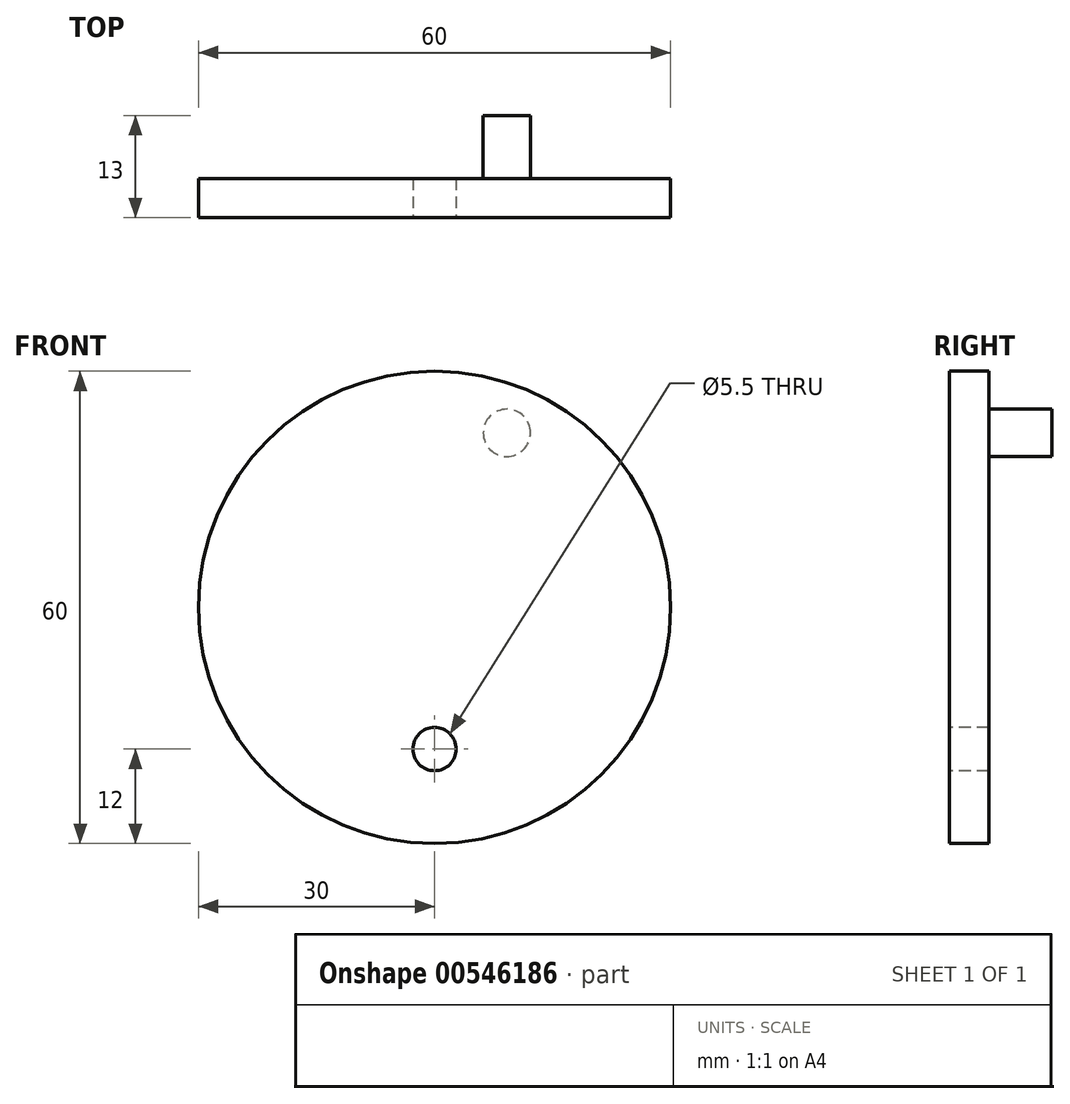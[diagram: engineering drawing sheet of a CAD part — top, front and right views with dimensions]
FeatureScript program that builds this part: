
annotation { "Feature Type Name" : "Feature", "Feature Type Description" : "" }
export const myFeature = defineFeature(function(context is Context, id is Id, definition is map)
    precondition{}
    {
        {
            var Q0;
            Q0=qCreatedBy(makeId("Front.planeOp"),FACE);
            var sketch = newSketch(context, id + "F0", { "sketchPlane" : qUnion([Q0])});
            skCircle(sketch, "E0", {"center": v(0, 0) * mm, "radius": 30 * mm});
            skSolve(sketch);
        }
        {
            var Q0;
            Q0 = qSketchRegion(id + "F0", true);
            extrude(context, id + "F1", {"entities" : qUnion([Q0]), "depth" : 5 * mm, "offsetDistance" : 25 * mm});
        }
        {
            var Q0;
            Q0=makeQuery(id+"F1.opExtrude","CAP_FACE",FACE,{"disambiguationData":[OSD([sQuery(id+"F0.wireOp",EDGE,"E0")])],"isStart":false});
            var sketch = newSketch(context, id + "F2", { "sketchPlane" : qUnion([Q0])});
            skLineSegment(sketch, "E1", {"start": v(0, 0) * mm, "end": v(0, -18) * mm});
            skCircle(sketch, "E2", {"center": v(0, -18) * mm, "radius": 2.75 * mm});
            skSolve(sketch);
        }
        {
            var Q0;
            Q0=makeQuery(id+"F2.imprint","IMPRINT",FACE,{"disambiguationData":[TD([[makeQuery(id+"F2.imprint","IMPRINT",EDGE,{"derivedFrom":sQuery(id+"F2.wireOp",EDGE,"tPdcvkMc-Bunr-VTIq-aCWn-UR4HdvMpEIR7")}),1.0]])]});
            var Q1;
            Q1=makeQuery(id+"F2.imprint","IMPRINT",FACE,{"disambiguationData":[TD([[makeQuery(id+"F2.imprint","IMPRINT",EDGE,{"derivedFrom":sQuery(id+"F2.wireOp",EDGE,"E2")}),1.0]])]});
            extrude(context, id + "F3", {"entities" : qUnion([Q0, Q1]), "operationType" : NewBodyOperationType.REMOVE, "oppositeDirection" : true, "depth" : 25 * mm, "offsetDistance" : 25 * mm});
        }
        {
            var Q0;
            Q0=makeQuery(id+"F1.opExtrude","CAP_FACE",FACE,{"disambiguationData":[OSD([sQuery(id+"F0.wireOp",EDGE,"E0")])],"isStart":true});
            var sketch = newSketch(context, id + "F4", { "sketchPlane" : qUnion([Q0])});
            skCircle(sketch, "E3", {"center": v(-9.18, 22.17) * mm, "radius": 3 * mm});
            skLineSegment(sketch, "E4", {"start": v(0, 0) * mm, "end": v(-9.18, 22.17) * mm});
            skSolve(sketch);
        }
        {
            var Q0;
            Q0 = qSketchRegion(id + "F4", true);
            extrude(context, id + "F5", {"entities" : qUnion([Q0]), "operationType" : NewBodyOperationType.ADD, "depth" : 8 * mm, "offsetDistance" : 25 * mm});
        }
    });
